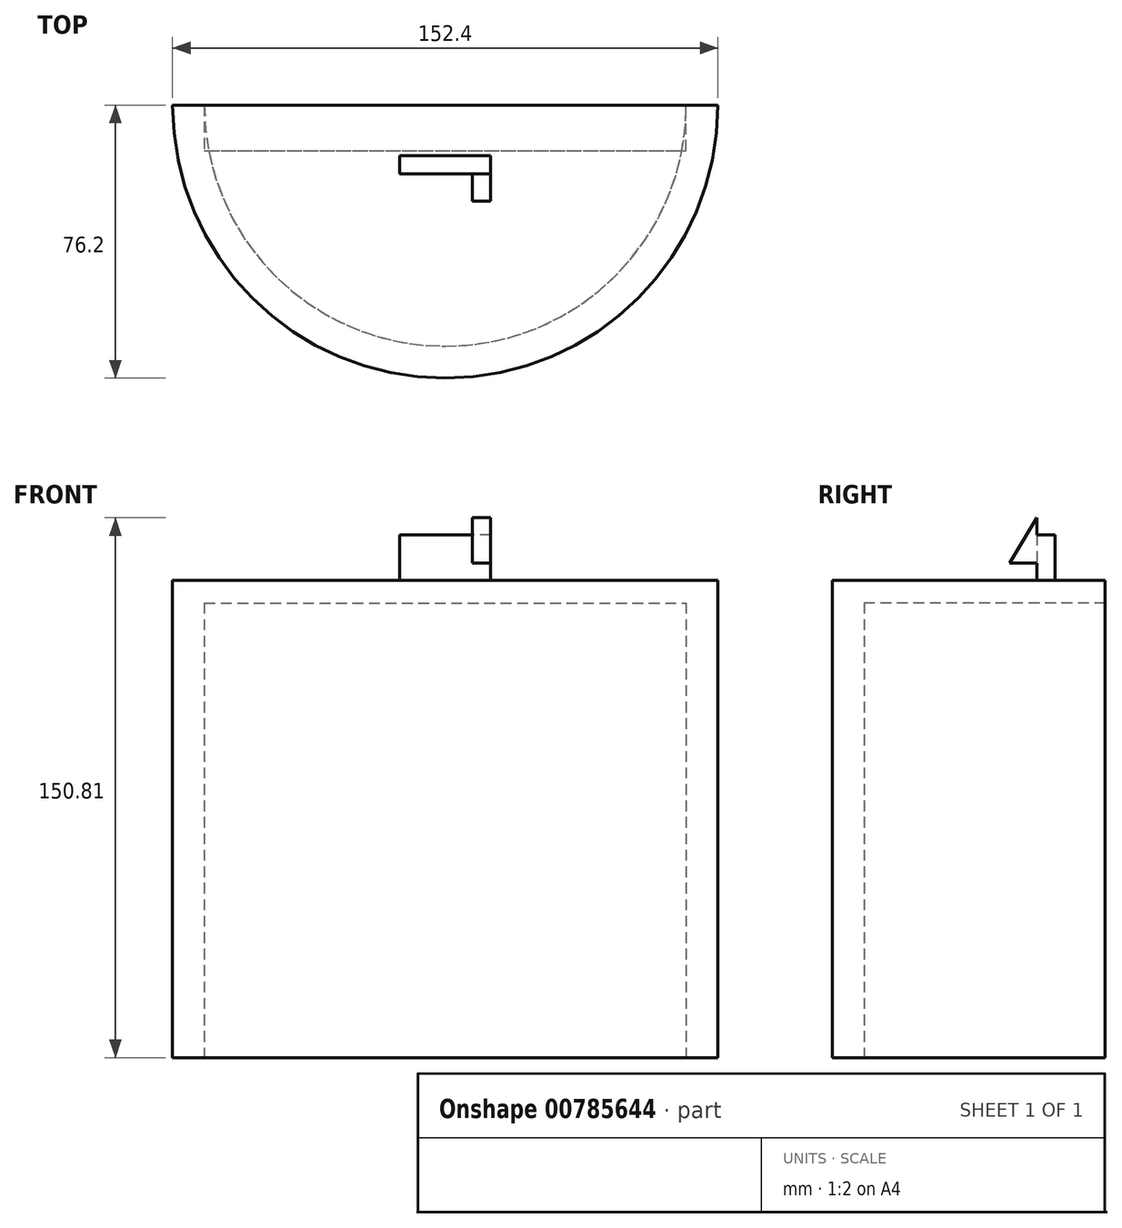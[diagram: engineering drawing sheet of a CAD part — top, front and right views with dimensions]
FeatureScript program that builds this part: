
annotation { "Feature Type Name" : "Feature", "Feature Type Description" : "" }
export const myFeature = defineFeature(function(context is Context, id is Id, definition is map)
    precondition{}
    {
        {
            var Q0;
            Q0=qCreatedBy(makeId("Top.planeOp"),FACE);
            var sketch = newSketch(context, id + "F0", { "sketchPlane" : qUnion([Q0])});
            skArc(sketch, "E0", {"start": v(76.2, 0) * mm, "mid": v(0, -76.2) * mm, "end": v(-76.2, 0) * mm});
            skLineSegment(sketch, "E1", {"start": v(-67.31, 0) * mm, "end": v(-67.31, -12.7) * mm});
            skLineSegment(sketch, "E2", {"start": v(-67.31, -12.7) * mm, "end": v(67.31, -12.7) * mm});
            skLineSegment(sketch, "E3", {"start": v(67.31, -12.7) * mm, "end": v(67.31, 0) * mm});
            skLineSegment(sketch, "E4", {"start": v(67.31, 0) * mm, "end": v(76.2, 0) * mm});
            skLineSegment(sketch, "E5", {"start": v(-76.2, 0) * mm, "end": v(-67.31, 0) * mm});
            skSolve(sketch);
        }
        {
            var Q0;
            Q0=qSketchRegion(id+"F0",true);
            extrude(context, id + "F1", {"entities" : qUnion([Q0]), "depth" : 3 / 406.4 * mm, "offsetDistance" : 25.4 * mm});
        }
        {
            var Q0;
            Q0=makeQuery(id+"F1.opExtrude","CAP_FACE",FACE,{"disambiguationData":[OSD([sQuery(id+"F0.wireOp",EDGE,"E0"),sQuery(id+"F0.wireOp",EDGE,"E1"),sQuery(id+"F0.wireOp",EDGE,"E2"),sQuery(id+"F0.wireOp",EDGE,"E3"),sQuery(id+"F0.wireOp",EDGE,"E4"),sQuery(id+"F0.wireOp",EDGE,"E5")])],"isStart":false});
            var sketch = newSketch(context, id + "F2", { "sketchPlane" : qUnion([Q0])});
            skArc(sketch, "E6", {"start": v(-76.2, 0) * mm, "mid": v(0, -76.2) * mm, "end": v(76.2, 0) * mm});
            skArc(sketch, "E7", {"start": v(-67.31, 0) * mm, "mid": v(0, -67.31) * mm, "end": v(67.31, 0) * mm});
            skLineSegment(sketch, "E8", {"start": v(-67.31, 0) * mm, "end": v(-76.2, 0) * mm});
            skLineSegment(sketch, "E9", {"start": v(67.31, 0) * mm, "end": v(76.2, 0) * mm});
            skSolve(sketch);
        }
        {
            var Q0;
            Q0=qSketchRegion(id+"F2",true);
            extrude(context, id + "F3", {"entities" : qUnion([Q0]), "operationType" : NewBodyOperationType.ADD, "depth" : 127 * mm, "offsetDistance" : 25.4 * mm});
        }
        {
            var Q0;
            Q0=makeQuery(id+"F3.opExtrude","CAP_FACE",FACE,{"disambiguationData":[OSD([sQuery(id+"F2.wireOp",EDGE,"E6"),sQuery(id+"F2.wireOp",EDGE,"E7"),sQuery(id+"F2.wireOp",EDGE,"E8"),sQuery(id+"F2.wireOp",EDGE,"E9")])],"isStart":false});
            var sketch = newSketch(context, id + "F4", { "sketchPlane" : qUnion([Q0])});
            skArc(sketch, "E10", {"start": v(-76.2, 0) * mm, "mid": v(0, -76.2) * mm, "end": v(76.2, 0) * mm});
            skLineSegment(sketch, "E11", {"start": v(-76.2, 0) * mm, "end": v(76.2, 0) * mm});
            skSolve(sketch);
        }
        {
            var Q0;
            Q0=qSketchRegion(id+"F4",true);
            extrude(context, id + "F5", {"entities" : qUnion([Q0]), "operationType" : NewBodyOperationType.ADD, "depth" : 6.35 * mm, "offsetDistance" : 25.4 * mm});
        }
        {
            var Q0;
            Q0=makeQuery(id+"F5.opExtrude","CAP_FACE",FACE,{"disambiguationData":[OSD([sQuery(id+"F4.wireOp",EDGE,"E10"),sQuery(id+"F4.wireOp",EDGE,"E11")])],"isStart":false});
            var sketch = newSketch(context, id + "F6", { "sketchPlane" : qUnion([Q0])});
            skLineSegment(sketch, "E12", {"start": v(-33.63, 0) * mm, "end": v(36.5, 0) * mm, "construction": true});
            skLineSegment(sketch, "E13", {"start": v(0, 0) * mm, "end": v(0, -25.4) * mm, "construction": true});
            skLineSegment(sketch, "E14", {"start": v(0, -14.09) * mm, "end": v(-12.7, -14.09) * mm});
            skLineSegment(sketch, "E15", {"start": v(-12.7, -14.09) * mm, "end": v(-12.7, -19.17) * mm});
            skLineSegment(sketch, "E16", {"start": v(0, -19.17) * mm, "end": v(-12.7, -19.17) * mm});
            skLineSegment(sketch, "E17.MirrorCS", {"start": v(0, -19.17) * mm, "end": v(12.7, -19.17) * mm});
            skLineSegment(sketch, "E18.MirrorCS", {"start": v(0, -14.09) * mm, "end": v(12.7, -14.09) * mm});
            skLineSegment(sketch, "E19.MirrorCS", {"start": v(12.7, -14.09) * mm, "end": v(12.7, -19.17) * mm});
            skSolve(sketch);
        }
        {
            var Q0;
            Q0=qSketchRegion(id+"F6",true);
            extrude(context, id + "F7", {"entities" : qUnion([Q0]), "operationType" : NewBodyOperationType.ADD, "depth" : 12.7 * mm, "offsetDistance" : 25.4 * mm});
        }
        {
            var Q0;
            Q0=makeQuery(id+"F7.opExtrude","SWEPT_FACE",FACE,{"disambiguationData":[OSD([sQuery(id+"F6.wireOp",EDGE,"E19.MirrorCS")])]});
            var sketch = newSketch(context, id + "F8", { "sketchPlane" : qUnion([Q0])});
            skLineSegment(sketch, "E20", {"start": v(-14.09, 138.11) * mm, "end": v(-26.79, 138.11) * mm, "construction": true});
            skLineSegment(sketch, "E21", {"start": v(-26.79, 138.11) * mm, "end": v(-19.17, 150.81) * mm});
            skLineSegment(sketch, "E22", {"start": v(-19.17, 150.81) * mm, "end": v(-19.17, 138.11) * mm});
            skLineSegment(sketch, "E23", {"start": v(-19.17, 138.11) * mm, "end": v(-26.79, 138.11) * mm});
            skSolve(sketch);
        }
        {
            var Q0;
            Q0=qSketchRegion(id+"F8",true);
            extrude(context, id + "F9", {"entities" : qUnion([Q0]), "operationType" : NewBodyOperationType.ADD, "oppositeDirection" : true, "depth" : 5.08 * mm, "offsetDistance" : 25.4 * mm});
        }
        {
            var Q0;
            Q0=qCreatedBy(makeId("Right.planeOp"),FACE);
            var sketch = newSketch(context, id + "F10", { "sketchPlane" : qUnion([Q0])});
            skLineSegment(sketch, "E24", {"start": v(0, 0) * mm, "end": v(-76.2, 0) * mm, "construction": true});
            skLineSegment(sketch, "E25", {"start": v(-69.5, 0) * mm, "end": v(-98.69, -24.5) * mm});
            skLineSegment(sketch, "E26", {"start": v(-76.2, 5.16) * mm, "end": v(-104.3, -17.81) * mm});
            skLineSegment(sketch, "E27", {"start": v(-104.3, -17.81) * mm, "end": v(-98.69, -24.5) * mm});
            skLineSegment(sketch, "E28", {"start": v(-76.2, 5.16) * mm, "end": v(-76.2, 0) * mm});
            skLineSegment(sketch, "E29", {"start": v(-76.2, 0) * mm, "end": v(-69.5, 0) * mm});
            skSolve(sketch);
        }
        {
            var Q0;
            Q0=makeQuery(id+"F10.imprint","IMPRINT",FACE,{"disambiguationData":[TD([[makeQuery(id+"F10.imprint","IMPRINT",EDGE,{"derivedFrom":sQuery(id+"F10.wireOp",EDGE,"E25")}),-1.0]])]});
            var Q1;
            Q1=makeQuery(id+"F5.boolean.opBoolean","MERGE",FACE,{"derivedFrom":[makeQuery(id+"F3.boolean.opBoolean","MERGE",FACE,{"derivedFrom":[makeQuery(id+"F1.opExtrude","SWEPT_FACE",FACE,{"disambiguationData":[OSD([sQuery(id+"F0.wireOp",EDGE,"E0")])]}),makeQuery(id+"F3.opExtrude","SWEPT_FACE",FACE,{"disambiguationData":[OSD([sQuery(id+"F2.wireOp",EDGE,"E6")])]})]}),makeQuery(id+"F5.opExtrude","SWEPT_FACE",FACE,{"disambiguationData":[OSD([sQuery(id+"F4.wireOp",EDGE,"E10")])]})]});
            revolve(context, id + "F11", {"surfaceOperationType" : NewSurfaceOperationType.NEW, "entities" : qUnion([Q0]), "axis" : qUnion([Q1]), "revolveType" : RevolveType.TWO_DIRECTIONS, "angle" : 20 * degree, "angleBack" : 340 * degree});
        }
        {
            var Q0;
            Q0=makeQuery(id+"F11.opRevolve","CAP_EDGE",EDGE,{"disambiguationData":[OSD([sQuery(id+"F10.wireOp",EDGE,"E27")])],"isStart":true});
            var Q1;
            Q1=makeQuery(id+"F11.opRevolve","CAP_EDGE",EDGE,{"disambiguationData":[OSD([sQuery(id+"F10.wireOp",EDGE,"E27")])],"isStart":false});
            fillet(context, id + "F12", {"entities" : qUnion([Q0, Q1]), "radius" : 5.08 * mm, "tangentPropagation" : true, "allowEdgeOverflow" : false});
        }
        {
            var Q0;
            Q0=makeQuery(id+"F11.opRevolve","SWEPT_BODY",BODY,{"disambiguationData":[OSD([sQuery(id+"F10.wireOp",EDGE,"E25"),sQuery(id+"F10.wireOp",EDGE,"E26"),sQuery(id+"F10.wireOp",EDGE,"E27"),sQuery(id+"F10.wireOp",EDGE,"E28"),sQuery(id+"F10.wireOp",EDGE,"E29")])]});
            deleteBodies(context, id + "F13", {"entities" : qUnion([Q0])});
        }
    });
